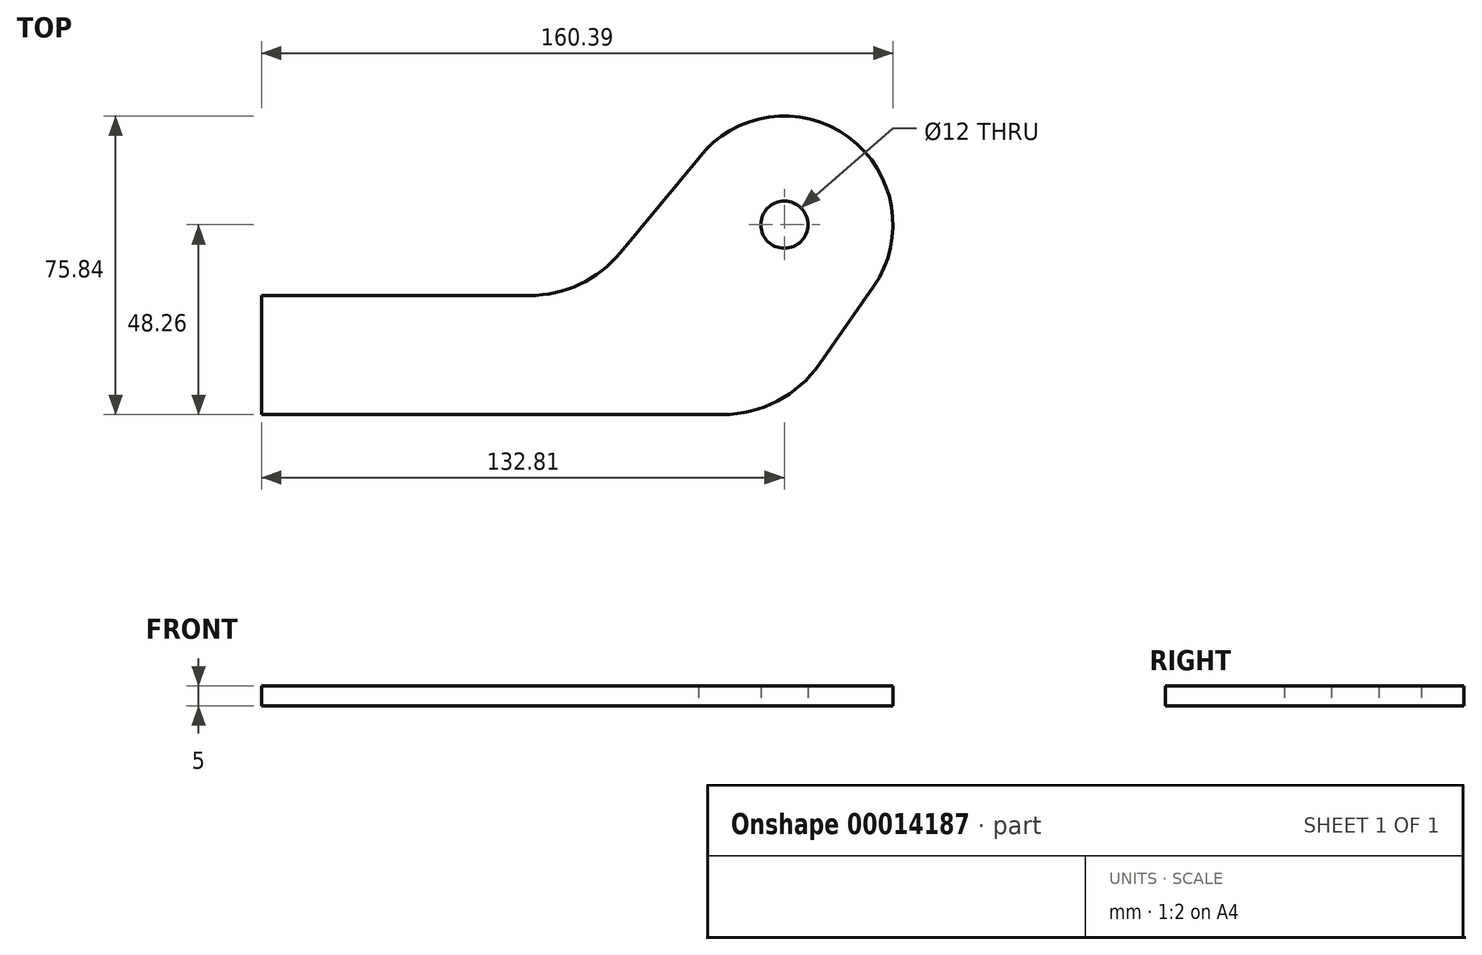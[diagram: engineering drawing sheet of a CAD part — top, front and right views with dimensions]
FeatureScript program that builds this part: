
annotation { "Feature Type Name" : "Feature", "Feature Type Description" : "" }
export const myFeature = defineFeature(function(context is Context, id is Id, definition is map)
    precondition{}
    {
        {
            var Q0;
            Q0=qCreatedBy(makeId("Top.planeOp"),FACE);
            var sketch = newSketch(context, id + "F0", { "sketchPlane" : qUnion([Q0])});
            skCircle(sketch, "E0", {"center": v(0, 0) * mm, "radius": 6 * mm});
            skLineSegment(sketch, "E1.top", {"start": v(-15.67, -48.26) * mm, "end": v(-132.81, -48.26) * mm});
            skLineSegment(sketch, "E1.right", {"start": v(-132.81, -18) * mm, "end": v(-132.81, -48.26) * mm});
            skArc(sketch, "E2", {"start": v(22.63, -15.76) * mm, "mid": v(16.28, 22.26) * mm, "end": v(-21.88, 16.79) * mm});
            skLineSegment(sketch, "E3", {"start": v(-21.88, 16.79) * mm, "end": v(-41.62, -7.1) * mm});
            skLineSegment(sketch, "E4", {"start": v(8.95, -35.4) * mm, "end": v(22.63, -15.76) * mm});
            skLineSegment(sketch, "E5.trimOffspring", {"start": v(-64.75, -18) * mm, "end": v(-132.81, -18) * mm});
            skPoint(sketch, "E6.visualSharp", {"position": v(-50.62, -18) * mm});
            skArc(sketch, "E6.filletArc", {"start": v(-64.75, -18) * mm, "mid": v(-51.96, -15.14) * mm, "end": v(-41.62, -7.1) * mm});
            skPoint(sketch, "E7.visualSharp", {"position": v(0, -48.26) * mm});
            skArc(sketch, "E7.filletArc", {"start": v(-15.67, -48.26) * mm, "mid": v(-1.78, -44.85) * mm, "end": v(8.95, -35.4) * mm});
            skSolve(sketch);
        }
        {
            var Q0;
            Q0 = qSketchRegion(id + "F0", true);
            extrude(context, id + "F1", {"entities" : qUnion([Q0]), "depth" : 5 * mm});
        }
    });
